# Revit family: Seating_Inc-Corner_Connecting_Table-Cobra-1
name_source: partatom
category: Furniture
revit_build: Autodesk Revit 2014 (Build: 20130308_1515(x64)
units: mm (PartAtom-declared; Revit-internal decimal feet)

## types (4) — shared parameters
Assembly Code = E2020200
Depth = 30"
Edge Finish = STI - Wood
Glide Finish = STI - Plastic Black
Height = 16"
Keynote = 12500
Low Emitting Finish = Yes
Low Emitting Material = Yes
Manufacturer = Seating Inc
Salvage or Reuse = Yes
Top Fenish = STI - Wood
Type Comments = Cobra Tables
URL = www.seatinginc.com
Width = 30"
zero-valued in all types: Percentage of Recycled Content

## per-type parameters (varying)
| type | Description | Edge Radius | Edge Square | Leg Finish | Support Finish | Top Radius | Top Square |
| CCT05-16B | Corner Radius Connecting Table
with (1) Black 16" Height Leg
and (4) Attachment Brackets | Yes | No | STI - Power Coat, Black | STI - Power Coat, Black | Yes | No |
| CCT05-16S | Corner Radius Connecting Table
with (1) Silver 16" Height Leg
and (4) Attachment Brackets | Yes | No | STI - Power Coat, Silver | STI - Power Coat, Silver | Yes | No |
| CCT06-16B | Corner Square Connecting Table
with (1) Black 16" Height Leg
and (4) Attachment Brackets | No | Yes | STI - Power Coat, Black | STI - Power Coat, Black | No | Yes |
| CCT06-16S | Corner Square Connecting Table
with (1) Silver 16" Height Leg
and (4) Attachment Brackets | No | Yes | STI - Power Coat, Silver | STI - Power Coat, Silver | No | Yes |

note: column(s) folded — value = type name in every type: Model

## geometry (parser evidence)
native form markers: Sweep x5
no freeform markers — native parametric forms only
